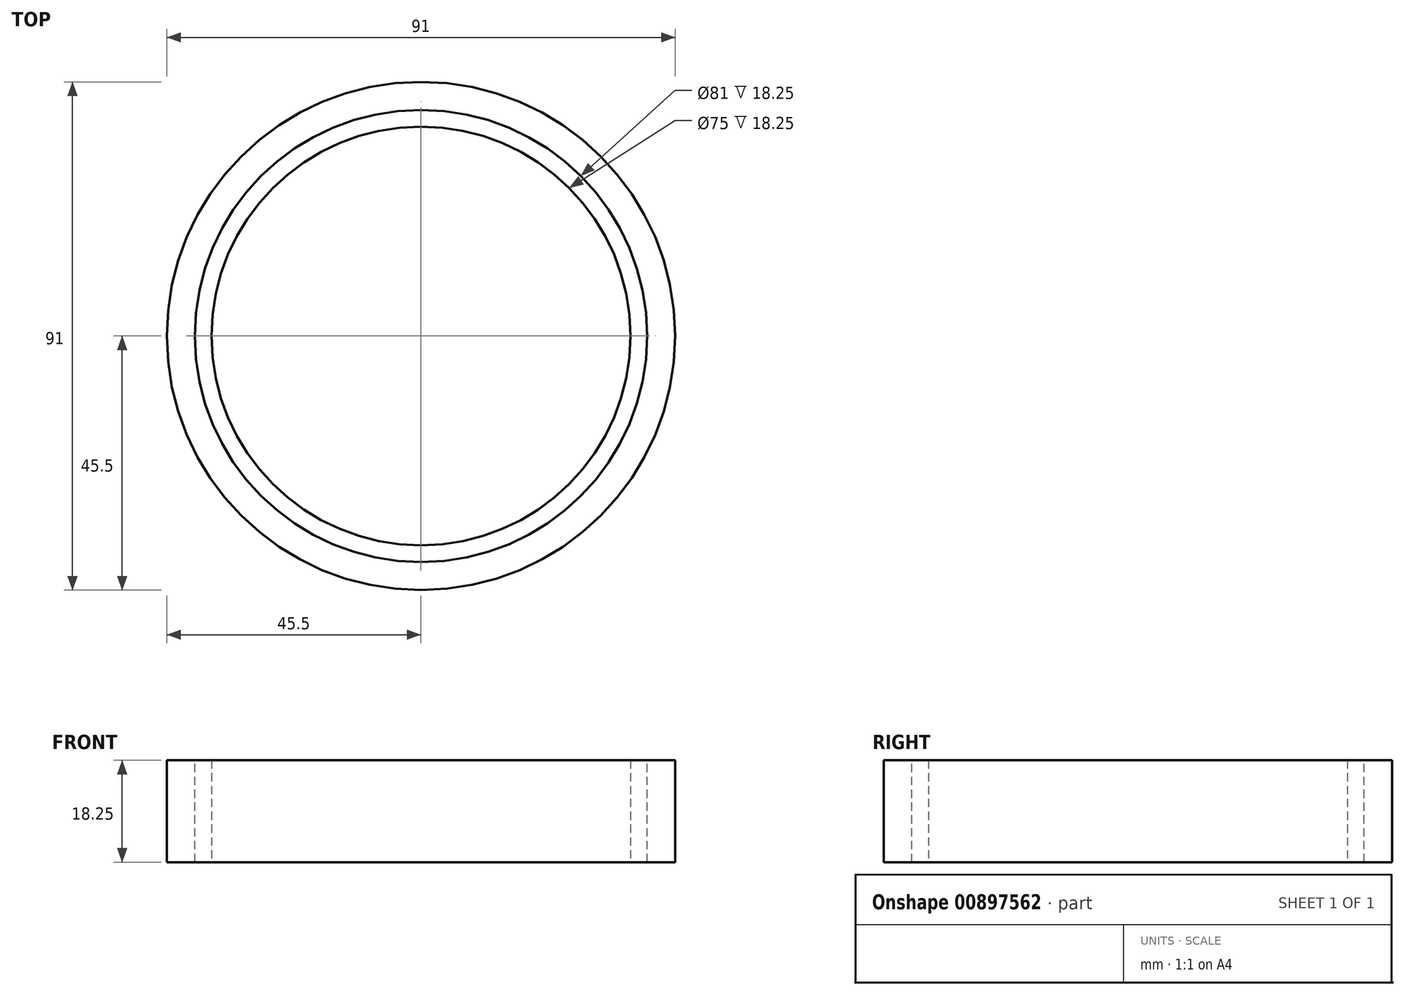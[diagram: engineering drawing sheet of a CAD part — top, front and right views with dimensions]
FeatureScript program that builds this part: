
annotation { "Feature Type Name" : "Feature", "Feature Type Description" : "" }
export const myFeature = defineFeature(function(context is Context, id is Id, definition is map)
    precondition{}
    {
        {
            var Q0;
            Q0=qCreatedBy(makeId("Top.planeOp"),FACE);
            var sketch = newSketch(context, id + "F0", { "sketchPlane" : qUnion([Q0])});
            skCircle(sketch, "E0", {"center": v(0, 0) * mm, "radius": 37.5 * mm});
            skCircle(sketch, "E1.0", {"center": v(0, 0) * mm, "radius": 40.5 * mm});
            skSolve(sketch);
        }
        {
            var Q0;
            Q0 = qSketchRegion(id + "F0", true);
            extrude(context, id + "F1", {"entities" : qUnion([Q0]), "depth" : 18.25 * mm, "offsetDistance" : 25 * mm});
        }
        {
            var Q0;
            Q0=makeQuery(id+"F1.opExtrude","CAP_FACE",FACE,{"disambiguationData":[OSD([sQuery(id+"F0.wireOp",EDGE,"E0"),sQuery(id+"F0.wireOp",EDGE,"E1.0")])],"isStart":false});
            var sketch = newSketch(context, id + "F2", { "sketchPlane" : qUnion([Q0])});
            skCircle(sketch, "E2", {"center": v(0, 0) * mm, "radius": 45.5 * mm});
            skCircle(sketch, "E3.0", {"center": v(0, 0) * mm, "radius": 40.5 * mm});
            skSolve(sketch);
        }
        {
            var Q0;
            Q0 = qSketchRegion(id + "F2", true);
            var Q1;
            Q1=makeQuery(id+"F1.opExtrude","CAP_FACE",FACE,{"disambiguationData":[OSD([sQuery(id+"F0.wireOp",EDGE,"E0"),sQuery(id+"F0.wireOp",EDGE,"E1.0")])],"isStart":true});
            extrude(context, id + "F3", {"entities" : qUnion([Q0]), "endBound" : BoundingType.UP_TO_SURFACE, "oppositeDirection" : true, "depth" : 25 * mm, "endBoundEntityFace" : qUnion([Q1]), "offsetDistance" : 25 * mm});
        }
    });
